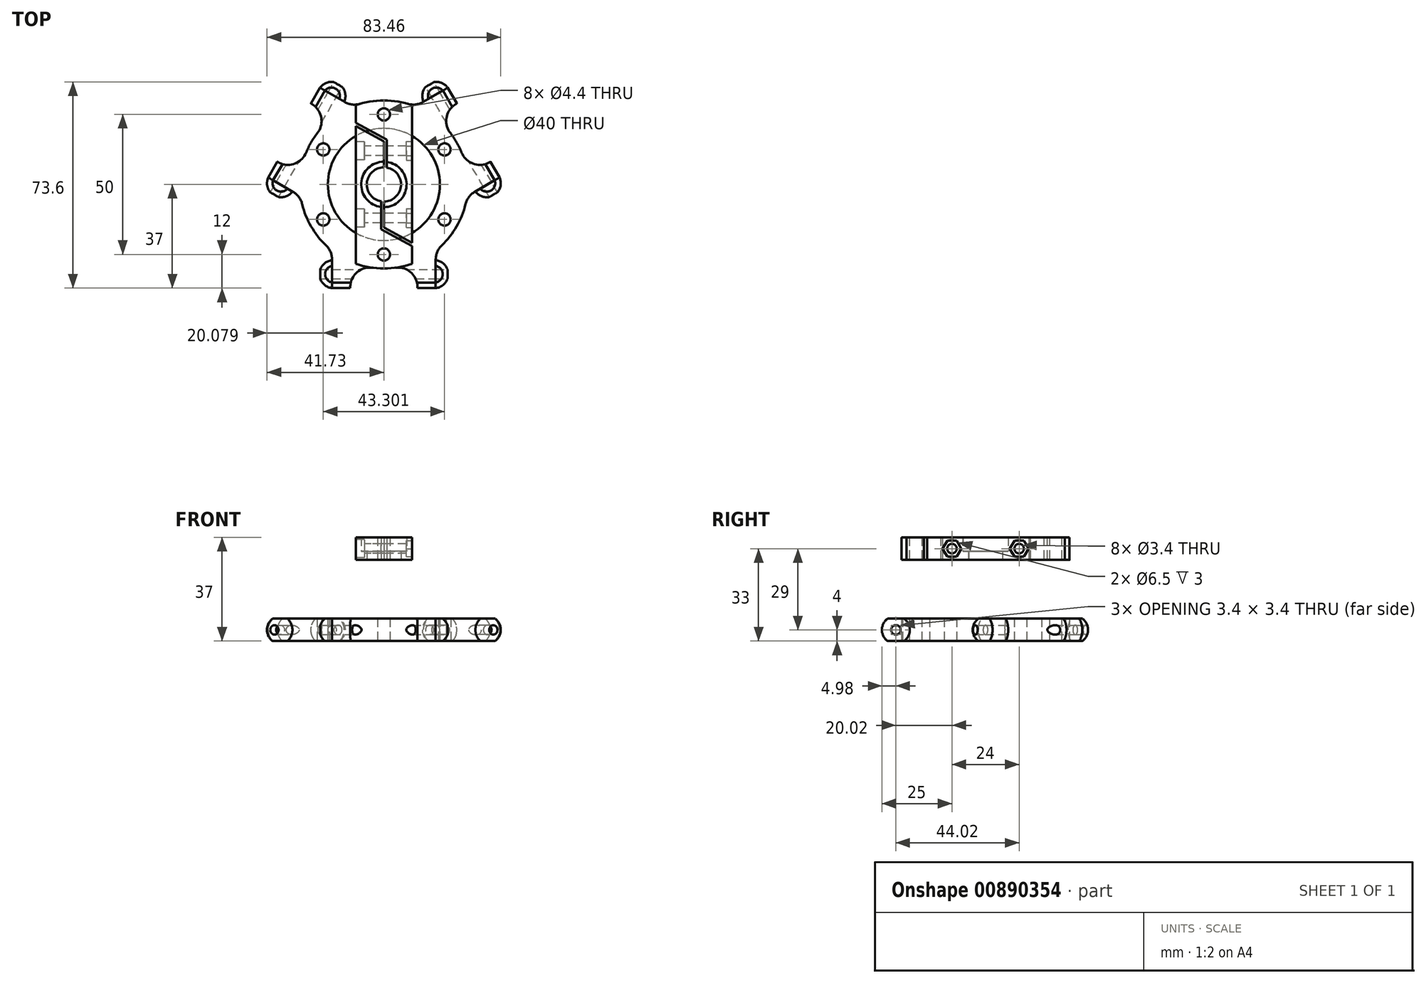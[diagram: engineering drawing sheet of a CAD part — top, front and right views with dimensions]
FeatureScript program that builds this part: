
annotation { "Feature Type Name" : "Feature", "Feature Type Description" : "" }
export const myFeature = defineFeature(function(context is Context, id is Id, definition is map)
    precondition{}
    {
        {
            var Q0;
            Q0=qCreatedBy(makeId("Top.planeOp"),FACE);
            var sketch = newSketch(context, id + "F0", { "sketchPlane" : qUnion([Q0])});
            skLineSegment(sketch, "E0", {"start": v(-16.34, 35.93) * mm, "end": v(-39.06, -3.47) * mm, "construction": true});
            skLineSegment(sketch, "E1", {"start": v(-40.4, -2.74) * mm, "end": v(-37.72, -4.2) * mm, "construction": true});
            skLineSegment(sketch, "E2", {"start": v(-17.63, 36.7) * mm, "end": v(-15.06, 35.15) * mm, "construction": true});
            skCircle(sketch, "E3", {"center": v(0, 0) * mm, "radius": 30 * mm});
            skCircle(sketch, "E4", {"center": v(0, 0) * mm, "radius": 20 * mm});
            skLineSegment(sketch, "E5", {"start": v(0, 0) * mm, "end": v(0, -43.55) * mm, "construction": true});
            skLineSegment(sketch, "E6", {"start": v(-25.45, -32) * mm, "end": v(35.74, -32) * mm, "construction": true});
            skLineSegment(sketch, "E7", {"start": v(-12, -37) * mm, "end": v(-12, -27.5) * mm});
            skLineSegment(sketch, "E8", {"start": v(-12, -37) * mm, "end": v(-18.5, -37) * mm});
            skLineSegment(sketch, "E9", {"start": v(-18.5, -37) * mm, "end": v(-18.5, -23.62) * mm});
            skLineSegment(sketch, "E10.MirrorCS", {"start": v(18.5, -37) * mm, "end": v(18.5, -23.62) * mm});
            skLineSegment(sketch, "E11.MirrorCS", {"start": v(12, -37) * mm, "end": v(12, -27.5) * mm});
            skLineSegment(sketch, "E12.MirrorCS", {"start": v(12, -37) * mm, "end": v(18.5, -37) * mm});
            skLineSegment(sketch, "E13.1.0", {"start": v(41.29, 2.48) * mm, "end": v(29.7, -4.21) * mm});
            skLineSegment(sketch, "E13.1.1", {"start": v(38.04, 8.1) * mm, "end": v(41.29, 2.48) * mm});
            skLineSegment(sketch, "E13.1.2", {"start": v(38.04, 8.1) * mm, "end": v(29.81, 3.36) * mm});
            skLineSegment(sketch, "E13.1.3", {"start": v(26.04, 28.9) * mm, "end": v(17.81, 24.14) * mm});
            skLineSegment(sketch, "E13.1.4", {"start": v(26.04, 28.9) * mm, "end": v(22.79, 34.52) * mm});
            skLineSegment(sketch, "E13.1.5", {"start": v(22.79, 34.52) * mm, "end": v(11.2, 27.83) * mm});
            skLineSegment(sketch, "E13.2.0", {"start": v(-22.79, 34.52) * mm, "end": v(-11.2, 27.83) * mm});
            skLineSegment(sketch, "E13.2.1", {"start": v(-26.04, 28.9) * mm, "end": v(-22.79, 34.52) * mm});
            skLineSegment(sketch, "E13.2.2", {"start": v(-26.04, 28.9) * mm, "end": v(-17.81, 24.14) * mm});
            skLineSegment(sketch, "E13.2.3", {"start": v(-38.04, 8.1) * mm, "end": v(-29.81, 3.36) * mm});
            skLineSegment(sketch, "E13.2.4", {"start": v(-38.04, 8.1) * mm, "end": v(-41.29, 2.48) * mm});
            skLineSegment(sketch, "E13.2.5", {"start": v(-41.29, 2.48) * mm, "end": v(-29.7, -4.21) * mm});
            skCircle(sketch, "E14", {"center": v(0, 25) * mm, "radius": 2.2 * mm});
            skCircle(sketch, "E15.1.0", {"center": v(-21.65, 12.5) * mm, "radius": 2.2 * mm});
            skCircle(sketch, "E15.2.0", {"center": v(-21.65, -12.5) * mm, "radius": 2.2 * mm});
            skCircle(sketch, "E15.3.0", {"center": v(0, -25) * mm, "radius": 2.2 * mm});
            skCircle(sketch, "E15.4.0", {"center": v(21.65, -12.5) * mm, "radius": 2.2 * mm});
            skCircle(sketch, "E15.5.0", {"center": v(21.65, 12.5) * mm, "radius": 2.2 * mm});
            skSolve(sketch);
        }
        {
            var Q0;
            Q0 = qSketchRegion(id + "F0", true);
            extrude(context, id + "F1", {"entities" : qUnion([Q0]), "endBound" : BoundingType.SYMMETRIC, "depth" : 10 * mm, "offsetDistance" : 25 * mm});
        }
        {
            var Q0;
            Q0=qCreatedBy(makeId("Top.planeOp"),FACE);
            var sketch = newSketch(context, id + "F2", { "sketchPlane" : qUnion([Q0])});
            skArc(sketch, "E16", {"start": v(-23, -32.02) * mm, "mid": v(-21.7, -35.37) * mm, "end": v(-18.5, -37) * mm});
            skLineSegment(sketch, "E17", {"start": v(-18, -32.02) * mm, "end": v(-25.15, -32.02) * mm, "construction": true});
            skLineSegment(sketch, "E18", {"start": v(0, 0) * mm, "end": v(0, -44.37) * mm, "construction": true});
            skLineSegment(sketch, "E19", {"start": v(-39.92, 23.05) * mm, "end": v(0, 0) * mm, "construction": true});
            skLineSegment(sketch, "E20", {"start": v(0, 0) * mm, "end": v(41.5, 23.96) * mm, "construction": true});
            skLineSegment(sketch, "E21", {"start": v(-18.5, -37) * mm, "end": v(-18.5, -27.05) * mm});
            skLineSegment(sketch, "E22", {"start": v(-23, -32.02) * mm, "end": v(-18.5, -32.02) * mm});
            skArc(sketch, "E23.1.0", {"start": v(39.23, -3.9) * mm, "mid": v(41.49, -1.11) * mm, "end": v(41.29, 2.48) * mm});
            skLineSegment(sketch, "E23.1.1", {"start": v(39.23, -3.9) * mm, "end": v(36.98, -0.01) * mm});
            skArc(sketch, "E23.2.0", {"start": v(-16.23, 35.93) * mm, "mid": v(-19.78, 36.49) * mm, "end": v(-22.79, 34.52) * mm});
            skLineSegment(sketch, "E23.2.1", {"start": v(-16.23, 35.93) * mm, "end": v(-18.48, 32.03) * mm});
            skPoint(sketch, "E23.center", {"position": v(0, 0) * mm});
            skLineSegment(sketch, "E24.MirrorCS", {"start": v(23, -32.02) * mm, "end": v(18.5, -32.02) * mm});
            skLineSegment(sketch, "E25.MirrorCS", {"start": v(18, -32.02) * mm, "end": v(25.15, -32.02) * mm, "construction": true});
            skLineSegment(sketch, "E26.MirrorCS", {"start": v(18.5, -37) * mm, "end": v(18.5, -27.05) * mm});
            skArc(sketch, "E27.MirrorCS", {"start": v(23, -32.02) * mm, "mid": v(21.7, -35.37) * mm, "end": v(18.5, -37) * mm});
            skSolve(sketch);
        }
        {
            var Q0;
            Q0 = qSketchRegion(id + "F2", true);
            var Q1;
            Q1=sQuery(id+"F2.wireOp",EDGE,"E17");
            revolve(context, id + "F3", {"surfaceOperationType" : NewSurfaceOperationType.NEW, "entities" : qUnion([Q0]), "axis" : qUnion([Q1]), "revolveType" : RevolveType.FULL});
        }
        {
            var Q0;
            Q0=qCreatedBy(makeId("Right.planeOp"),FACE);
            var sketch = newSketch(context, id + "F4", { "sketchPlane" : qUnion([Q0])});
            skLineSegment(sketch, "E28", {"start": v(0, 32.68) * mm, "end": v(0, -16.38) * mm, "construction": true});
            skSolve(sketch);
        }
        {
            var Q0;
            Q0=makeQuery(id+"F3.opRevolve","SWEPT_BODY",BODY,{"disambiguationData":[OSD([sQuery(id+"F2.wireOp",EDGE,"E16"),sQuery(id+"F2.wireOp",EDGE,"E21"),sQuery(id+"F2.wireOp",EDGE,"E22")])]});
            var Q1;
            Q1=makeQuery(id+"F3.opRevolve","SWEPT_BODY",BODY,{"disambiguationData":[OSD([sQuery(id+"F2.wireOp",EDGE,"E24.MirrorCS"),sQuery(id+"F2.wireOp",EDGE,"E26.MirrorCS"),sQuery(id+"F2.wireOp",EDGE,"E27.MirrorCS")])]});
            var Q2;
            Q2=sQuery(id+"F4.wireOp",EDGE,"E28");
            circularPattern(context, id + "F5", {"entities" : qUnion([Q0, Q1]), "axis" : qUnion([Q2]), "angle" : 360 * degree, "instanceCount" : 3, "equalSpace" : true});
        }
        {
            var Q0;
            Q0=makeQuery(id+"F1.opExtrude","CAP_EDGE",EDGE,{"disambiguationData":[OSD([sQuery(id+"F0.wireOp",EDGE,"E13.2.1")])],"isStart":false});
            var Q1;
            Q1=makeQuery(id+"F1.opExtrude","CAP_EDGE",EDGE,{"disambiguationData":[OSD([sQuery(id+"F0.wireOp",EDGE,"E13.2.4")])],"isStart":false});
            var Q2;
            Q2=makeQuery(id+"F1.opExtrude","CAP_EDGE",EDGE,{"disambiguationData":[OSD([sQuery(id+"F0.wireOp",EDGE,"E13.1.4")])],"isStart":false});
            var Q3;
            Q3=makeQuery(id+"F1.opExtrude","CAP_EDGE",EDGE,{"disambiguationData":[OSD([sQuery(id+"F0.wireOp",EDGE,"E13.1.1")])],"isStart":false});
            var Q4;
            Q4=makeQuery(id+"F1.opExtrude","CAP_EDGE",EDGE,{"disambiguationData":[OSD([sQuery(id+"F0.wireOp",EDGE,"E12.MirrorCS")])],"isStart":false});
            var Q5;
            Q5=makeQuery(id+"F1.opExtrude","CAP_EDGE",EDGE,{"disambiguationData":[OSD([sQuery(id+"F0.wireOp",EDGE,"E8")])],"isStart":false});
            var Q6;
            Q6=makeQuery(id+"F1.opExtrude","CAP_EDGE",EDGE,{"disambiguationData":[OSD([sQuery(id+"F0.wireOp",EDGE,"E8")])],"isStart":true});
            var Q7;
            Q7=makeQuery(id+"F1.opExtrude","CAP_EDGE",EDGE,{"disambiguationData":[OSD([sQuery(id+"F0.wireOp",EDGE,"E12.MirrorCS")])],"isStart":true});
            var Q8;
            Q8=makeQuery(id+"F1.opExtrude","CAP_EDGE",EDGE,{"disambiguationData":[OSD([sQuery(id+"F0.wireOp",EDGE,"E13.1.1")])],"isStart":true});
            var Q9;
            Q9=makeQuery(id+"F1.opExtrude","CAP_EDGE",EDGE,{"disambiguationData":[OSD([sQuery(id+"F0.wireOp",EDGE,"E13.1.4")])],"isStart":true});
            var Q10;
            Q10=makeQuery(id+"F1.opExtrude","CAP_EDGE",EDGE,{"disambiguationData":[OSD([sQuery(id+"F0.wireOp",EDGE,"E13.2.1")])],"isStart":true});
            var Q11;
            Q11=makeQuery(id+"F1.opExtrude","CAP_EDGE",EDGE,{"disambiguationData":[OSD([sQuery(id+"F0.wireOp",EDGE,"E13.2.4")])],"isStart":true});
            fillet(context, id + "F6", {"entities" : qUnion([Q0, Q1, Q2, Q3, Q4, Q5, Q6, Q7, Q8, Q9, Q10, Q11]), "radius" : 5 * mm, "tangentPropagation" : true, "allowEdgeOverflow" : false});
        }
        {
            var Q0;
            Q0=qCreatedBy(makeId("Top.planeOp"),FACE);
            var sketch = newSketch(context, id + "F7", { "sketchPlane" : qUnion([Q0])});
            skCircle(sketch, "E29", {"center": v(0, 0) * mm, "radius": 54.32 * mm});
            skSolve(sketch);
        }
        {
            var Q0;
            Q0=makeQuery(id+"F7.imprint","IMPRINT",FACE,{"disambiguationData":[TD([[makeQuery(id+"F7.imprint","IMPRINT",EDGE,{"derivedFrom":sQuery(id+"F7.wireOp",EDGE,"E29")}),1.0]])]});
            extrude(context, id + "F8", {"entities" : qUnion([Q0]), "operationType" : NewBodyOperationType.REMOVE, "depth" : 10 * mm, "offsetDistance" : 25 * mm, "hasSecondDirection" : true, "secondDirectionOppositeDirection" : false, "secondDirectionDepth" : 4 * mm});
        }
        {
            var Q0;
            Q0=makeQuery(id+"F7.imprint","IMPRINT",FACE,{"disambiguationData":[TD([[makeQuery(id+"F7.imprint","IMPRINT",EDGE,{"derivedFrom":sQuery(id+"F7.wireOp",EDGE,"E29")}),1.0]])]});
            extrude(context, id + "F9", {"entities" : qUnion([Q0]), "operationType" : NewBodyOperationType.REMOVE, "oppositeDirection" : true, "depth" : 20 * mm, "offsetDistance" : 25 * mm, "hasSecondDirection" : true, "secondDirectionOppositeDirection" : true, "secondDirectionDepth" : 4 * mm});
        }
        {
            var Q0;
            Q0=qCreatedBy(makeId("Right.planeOp"),FACE);
            var sketch = newSketch(context, id + "F10", { "sketchPlane" : qUnion([Q0])});
            skCircle(sketch, "E30", {"center": v(-32.02, 0) * mm, "radius": 1.7 * mm});
            skSolve(sketch);
        }
        {
            var Q0;
            Q0 = qSketchRegion(id + "F10", true);
            extrude(context, id + "F11", {"entities" : qUnion([Q0]), "operationType" : NewBodyOperationType.REMOVE, "endBound" : BoundingType.SYMMETRIC, "oppositeDirection" : true, "depth" : 80 * mm, "offsetDistance" : 25 * mm});
        }
        {
            var Q0;
            Q0=sQuery(id+"F2.wireOp",EDGE,"E19");
            cPlane(context, id + "F12", {"entities" : qUnion([Q0]), "cplaneType" : CPlaneType.LINE_ANGLE, "offset" : 25 * mm, "angle" : 0 * degree, "width" : 150 * mm, "height" : 150 * mm});
        }
        {
            var Q0;
            Q0=qCreatedBy(id+"F12.planeOp",FACE);
            var sketch = newSketch(context, id + "F13", { "sketchPlane" : qUnion([Q0])});
            skCircle(sketch, "E31", {"center": v(32.02, 0) * mm, "radius": 1.7 * mm});
            skSolve(sketch);
        }
        {
            var Q0;
            Q0 = qSketchRegion(id + "F13", true);
            extrude(context, id + "F14", {"entities" : qUnion([Q0]), "operationType" : NewBodyOperationType.REMOVE, "endBound" : BoundingType.SYMMETRIC, "oppositeDirection" : true, "depth" : 80 * mm, "offsetDistance" : 25 * mm});
        }
        {
            var Q0;
            Q0=sQuery(id+"F2.wireOp",EDGE,"E20");
            cPlane(context, id + "F15", {"entities" : qUnion([Q0]), "cplaneType" : CPlaneType.LINE_ANGLE, "offset" : 25 * mm, "angle" : 0 * degree, "width" : 150 * mm, "height" : 150 * mm});
        }
        {
            var Q0;
            Q0=qCreatedBy(id+"F15.planeOp",FACE);
            var sketch = newSketch(context, id + "F16", { "sketchPlane" : qUnion([Q0])});
            skCircle(sketch, "E32", {"center": v(-32.02, 0) * mm, "radius": 1.7 * mm});
            skSolve(sketch);
        }
        {
            var Q0;
            Q0 = qSketchRegion(id + "F16", true);
            extrude(context, id + "F17", {"entities" : qUnion([Q0]), "operationType" : NewBodyOperationType.REMOVE, "endBound" : BoundingType.SYMMETRIC, "oppositeDirection" : true, "depth" : 80 * mm, "offsetDistance" : 25 * mm});
        }
        {
            var Q0;
            Q0=makeQuery(id+"F1.opExtrude","SWEPT_EDGE",EDGE,{"disambiguationData":[OSD([sQuery(id+"F0.wireOp",EDGE,"E3"),sQuery(id+"F0.wireOp",EDGE,"E13.2.0")])]});
            var Q1;
            Q1=makeQuery(id+"F1.opExtrude","SWEPT_EDGE",EDGE,{"disambiguationData":[OSD([sQuery(id+"F0.wireOp",EDGE,"E3"),sQuery(id+"F0.wireOp",EDGE,"E13.1.5")])]});
            var Q2;
            Q2=makeQuery(id+"F1.opExtrude","SWEPT_EDGE",EDGE,{"disambiguationData":[OSD([sQuery(id+"F0.wireOp",EDGE,"E3"),sQuery(id+"F0.wireOp",EDGE,"E13.1.0")])]});
            var Q3;
            Q3=makeQuery(id+"F1.opExtrude","SWEPT_EDGE",EDGE,{"disambiguationData":[OSD([sQuery(id+"F0.wireOp",EDGE,"E3"),sQuery(id+"F0.wireOp",EDGE,"E10.MirrorCS")])]});
            var Q4;
            Q4=makeQuery(id+"F1.opExtrude","SWEPT_EDGE",EDGE,{"disambiguationData":[OSD([sQuery(id+"F0.wireOp",EDGE,"E3"),sQuery(id+"F0.wireOp",EDGE,"E13.2.5")])]});
            var Q5;
            Q5=makeQuery(id+"F1.opExtrude","SWEPT_EDGE",EDGE,{"disambiguationData":[OSD([sQuery(id+"F0.wireOp",EDGE,"E3"),sQuery(id+"F0.wireOp",EDGE,"E9")])]});
            fillet(context, id + "F18", {"entities" : qUnion([Q0, Q1, Q2, Q3, Q4, Q5]), "radius" : 7 * mm, "tangentPropagation" : true, "allowEdgeOverflow" : false});
        }
        {
            var Q0;
            Q0=qCreatedBy(makeId("Top.planeOp"),FACE);
            cPlane(context, id + "F19", {"entities" : qUnion([Q0]), "cplaneType" : CPlaneType.OFFSET, "offset" : 25 * mm, "width" : 150 * mm, "height" : 150 * mm});
        }
        {
            var Q0;
            Q0=qCreatedBy(id+"F19.planeOp",FACE);
            var sketch = newSketch(context, id + "F20", { "sketchPlane" : qUnion([Q0])});
            skCircle(sketch, "E33", {"center": v(0, 25) * mm, "radius": 2.2 * mm});
            skCircle(sketch, "E34", {"center": v(0, -25) * mm, "radius": 2.2 * mm});
            skArc(sketch, "E35", {"start": v(10, 28.28) * mm, "mid": v(0, 30) * mm, "end": v(-10, 28.28) * mm});
            skLineSegment(sketch, "E36", {"start": v(-10, 28.28) * mm, "end": v(-10, -28.28) * mm});
            skLineSegment(sketch, "E37", {"start": v(10, -28.28) * mm, "end": v(10, 28.28) * mm});
            skArc(sketch, "E38.trimOffspring", {"start": v(-10, -28.28) * mm, "mid": v(0, -30) * mm, "end": v(10, -28.28) * mm});
            skSolve(sketch);
        }
        {
            var Q0;
            Q0=makeQuery(id+"F20.imprint","IMPRINT",FACE,{"disambiguationData":[TD([[makeQuery(id+"F20.imprint","IMPRINT",EDGE,{"derivedFrom":sQuery(id+"F20.wireOp",EDGE,"E33")}),-1.0]])]});
            extrude(context, id + "F21", {"entities" : qUnion([Q0]), "depth" : 8 * mm, "offsetDistance" : 25 * mm});
        }
        {
            var Q0;
            Q0=makeQuery(id+"F21.opExtrude","CAP_FACE",FACE,{"disambiguationData":[OSD([sQuery(id+"F20.wireOp",EDGE,"E33"),sQuery(id+"F20.wireOp",EDGE,"E34"),sQuery(id+"F20.wireOp",EDGE,"E35"),sQuery(id+"F20.wireOp",EDGE,"E36"),sQuery(id+"F20.wireOp",EDGE,"E37"),sQuery(id+"F20.wireOp",EDGE,"E38.trimOffspring")])],"isStart":true});
            var sketch = newSketch(context, id + "F22", { "sketchPlane" : qUnion([Q0])});
            skCircle(sketch, "E39", {"center": v(0, 0) * mm, "radius": 6.1 * mm});
            skCircle(sketch, "E40", {"center": v(0, 0) * mm, "radius": 8.1 * mm});
            skLineSegment(sketch, "E41", {"start": v(-10, -20.86) * mm, "end": v(0, -15.4) * mm});
            skLineSegment(sketch, "E42", {"start": v(1, 0) * mm, "end": v(1, -16) * mm});
            skLineSegment(sketch, "E43", {"start": v(1, -16) * mm, "end": v(-10, -22) * mm});
            skLineSegment(sketch, "E44", {"start": v(-10, -22) * mm, "end": v(10, -22) * mm, "construction": true});
            skLineSegment(sketch, "E45", {"start": v(-10, -22) * mm, "end": v(-10, -20.86) * mm});
            skLineSegment(sketch, "E46", {"start": v(0, -15.4) * mm, "end": v(0, 0) * mm});
            skLineSegment(sketch, "E47", {"start": v(0, 0) * mm, "end": v(1, 0) * mm});
            skLineSegment(sketch, "E48.1.0", {"start": v(10, 22) * mm, "end": v(10, 20.86) * mm});
            skLineSegment(sketch, "E48.1.1", {"start": v(10, 20.86) * mm, "end": v(0, 15.4) * mm});
            skLineSegment(sketch, "E48.1.2", {"start": v(-1, 16) * mm, "end": v(10, 22) * mm});
            skLineSegment(sketch, "E48.1.3", {"start": v(0, 15.4) * mm, "end": v(0, 0) * mm});
            skLineSegment(sketch, "E48.1.4", {"start": v(-1, 0) * mm, "end": v(-1, 16) * mm});
            skLineSegment(sketch, "E48.1.5", {"start": v(0, 0) * mm, "end": v(-1, 0) * mm});
            skSolve(sketch);
        }
        {
            var Q0;
            Q0=makeQuery(id+"F22.imprint","IMPRINT",FACE,{"disambiguationData":[TD([[makeQuery(id+"F22.imprint","IMPRINT",EDGE,{"derivedFrom":sQuery(id+"F22.wireOp",EDGE,"E39")}),1.0]])]});
            var Q1;
            Q1=makeQuery(id+"F21.opExtrude","CAP_FACE",FACE,{"disambiguationData":[OSD([sQuery(id+"F20.wireOp",EDGE,"E33"),sQuery(id+"F20.wireOp",EDGE,"E34"),sQuery(id+"F20.wireOp",EDGE,"E35"),sQuery(id+"F20.wireOp",EDGE,"E36"),sQuery(id+"F20.wireOp",EDGE,"E37"),sQuery(id+"F20.wireOp",EDGE,"E38.trimOffspring")])],"isStart":false});
            extrude(context, id + "F23", {"entities" : qUnion([Q0]), "operationType" : NewBodyOperationType.REMOVE, "endBound" : BoundingType.UP_TO_SURFACE, "oppositeDirection" : true, "depth" : 25 * mm, "endBoundEntityFace" : qUnion([Q1]), "offsetDistance" : 25 * mm});
        }
        {
            var Q0;
            Q0=makeQuery(id+"F22.imprint","IMPRINT",FACE,{"disambiguationData":[TD([[makeQuery(id+"F22.imprint","IMPRINT",EDGE,{"derivedFrom":sQuery(id+"F22.wireOp",EDGE,"E48.1.0")}),-1.0]])]});
            var Q1;
            {var subQ0=sQuery(id+"F22.wireOp",EDGE,"E48.1.4");var subQ1=sQuery(id+"F22.wireOp",EDGE,"E39");var subQ2=makeQuery(id+"F22.imprint","INTERSECT",VERTEX,{"derivedFrom":[subQ1,subQ0]});Q1=makeQuery(id+"F22.imprint","IMPRINT",FACE,{"disambiguationData":[TD([[makeQuery(id+"F22.imprint","IMPRINT",EDGE,{"disambiguationData":[TD([[subQ2,1.0]])],"derivedFrom":subQ1}),-1.0]])]});}
            var Q2;
            {var subQ1=sQuery(id+"F22.wireOp",EDGE,"E41");Q2=makeQuery(id+"F22.imprint","IMPRINT",FACE,{"disambiguationData":[TD([[makeQuery(id+"F22.imprint","IMPRINT",EDGE,{"derivedFrom":subQ1}),-1.0]])]});}
            var Q3;
            {var subQ0=sQuery(id+"F22.wireOp",EDGE,"E46");var subQ1=sQuery(id+"F22.wireOp",EDGE,"E39");var subQ2=makeQuery(id+"F22.imprint","INTERSECT",VERTEX,{"derivedFrom":[subQ1,subQ0]});Q3=makeQuery(id+"F22.imprint","IMPRINT",FACE,{"disambiguationData":[TD([[makeQuery(id+"F22.imprint","IMPRINT",EDGE,{"disambiguationData":[TD([[subQ2,-1.0]])],"derivedFrom":subQ1}),-1.0]])]});}
            var Q4;
            Q4=makeQuery(id+"F21.opExtrude","CAP_FACE",FACE,{"disambiguationData":[OSD([sQuery(id+"F20.wireOp",EDGE,"E33"),sQuery(id+"F20.wireOp",EDGE,"E34"),sQuery(id+"F20.wireOp",EDGE,"E35"),sQuery(id+"F20.wireOp",EDGE,"E36"),sQuery(id+"F20.wireOp",EDGE,"E37"),sQuery(id+"F20.wireOp",EDGE,"E38.trimOffspring")])],"isStart":false});
            extrude(context, id + "F24", {"entities" : qUnion([Q0, Q1, Q2, Q3]), "operationType" : NewBodyOperationType.REMOVE, "endBound" : BoundingType.UP_TO_SURFACE, "oppositeDirection" : true, "depth" : 25 * mm, "endBoundEntityFace" : qUnion([Q4]), "offsetDistance" : 25 * mm});
        }
        {
            var Q0;
            {var subQ3=sQuery(id+"F22.wireOp",EDGE,"00b420b3-74bb-4662-af47-3d81f60943aa.1.3");var subQ5=sQuery(id+"F22.wireOp",EDGE,"E40");var subQ6=makeQuery(id+"F22.imprint","INTERSECT",VERTEX,{"derivedFrom":[subQ5,subQ3]});Q0=makeQuery(id+"F22.imprint","IMPRINT",FACE,{"disambiguationData":[TD([[makeQuery(id+"F22.imprint","IMPRINT",EDGE,{"disambiguationData":[TD([[subQ6,-1.0]])],"derivedFrom":subQ5}),1.0]])]});}
            var Q1;
            {var subQ3=sQuery(id+"F22.wireOp",EDGE,"00b420b3-74bb-4662-af47-3d81f60943aa.1.2");var subQ5=sQuery(id+"F22.wireOp",EDGE,"E40");var subQ6=makeQuery(id+"F22.imprint","INTERSECT",VERTEX,{"derivedFrom":[subQ5,subQ3]});Q1=makeQuery(id+"F22.imprint","IMPRINT",FACE,{"disambiguationData":[TD([[makeQuery(id+"F22.imprint","IMPRINT",EDGE,{"disambiguationData":[TD([[subQ6,1.0]])],"derivedFrom":subQ5}),1.0]])]});}
            extrude(context, id + "F25", {"entities" : qUnion([Q0, Q1]), "operationType" : NewBodyOperationType.REMOVE, "oppositeDirection" : true, "depth" : 20 * mm, "offsetDistance" : 25 * mm, "hasSecondDirection" : true, "secondDirectionOppositeDirection" : true, "secondDirectionDepth" : 3 * mm});
        }
        {
            var Q0;
            {var subQ0=sQuery(id+"F20.wireOp",EDGE,"E38.trimOffspring");var subQ2=sQuery(id+"F20.wireOp",EDGE,"E36");Q0=makeQuery(id+"F24.boolean.opBoolean","SPLIT",FACE,{"disambiguationData":[TD([makeQuery(id+"F21.opExtrude","SWEPT_FACE",FACE,{"disambiguationData":[OSD([subQ0])]})])],"derivedFrom":makeQuery(id+"F21.opExtrude","SWEPT_FACE",FACE,{"disambiguationData":[OSD([subQ2])]})});}
            var sketch = newSketch(context, id + "F26", { "sketchPlane" : qUnion([Q0])});
            skPoint(sketch, "E49", {"position": v(-12, 29) * mm});
            skPoint(sketch, "E49.positionSnap0", {"position": v(-20.86, 29) * mm});
            skPoint(sketch, "E50", {"position": v(12, 29) * mm});
            skSolve(sketch);
        }
        {
            var Q0;
            Q0=sQuery(id+"F26.wireOp",VERTEX,"E49");
            var Q1;
            Q1=sQuery(id+"F26.wireOp",VERTEX,"E50");
            var Q2;
            Q2=makeQuery(id+"F24.boolean.opBoolean","SPLIT",BODY,{"disambiguationData":[OD(0.0)],"derivedFrom":makeQuery(id+"F21.opExtrude","SWEPT_BODY",BODY,{"disambiguationData":[OSD([sQuery(id+"F20.wireOp",EDGE,"E33"),sQuery(id+"F20.wireOp",EDGE,"E34"),sQuery(id+"F20.wireOp",EDGE,"E35"),sQuery(id+"F20.wireOp",EDGE,"E36"),sQuery(id+"F20.wireOp",EDGE,"E37"),sQuery(id+"F20.wireOp",EDGE,"E38.trimOffspring")])]})});
            var Q3;
            Q3=makeQuery(id+"F24.boolean.opBoolean","SPLIT",BODY,{"disambiguationData":[OD(1.0)],"derivedFrom":makeQuery(id+"F21.opExtrude","SWEPT_BODY",BODY,{"disambiguationData":[OSD([sQuery(id+"F20.wireOp",EDGE,"E33"),sQuery(id+"F20.wireOp",EDGE,"E34"),sQuery(id+"F20.wireOp",EDGE,"E35"),sQuery(id+"F20.wireOp",EDGE,"E36"),sQuery(id+"F20.wireOp",EDGE,"E37"),sQuery(id+"F20.wireOp",EDGE,"E38.trimOffspring")])]})});
            hole(context, id + "F27", {"style" : HoleStyle.C_BORE, "endStyle" : HoleEndStyle.THROUGH, "standardTappedOrClearance" : lookupTablePath({ "fit" : "Normal", "standard" : "ISO", "size" : "M3", "type" : "Clearance" }), "standardBlindInLast" : lookupTablePath({ "fit" : "Normal", "standard" : "ISO", "size" : "M3", "type" : "Clearance" }), "holeDiameter" : 3.4 * mm, "cBoreDiameter" : 6.5 * mm, "cBoreDepth" : 3 * mm, "majorDiameter" : 5 * mm, "isTappedThrough" : true, "tappedDepth" : 12 * mm, "tapClearance" : 3, "locations" : qUnion([Q0, Q1]), "scope" : qUnion([Q2, Q3])});
        }
        {
            var Q0;
            {var subQ1=sQuery(id+"F20.wireOp",EDGE,"E37");var subQ3=sQuery(id+"F20.wireOp",EDGE,"E35");Q0=makeQuery(id+"F24.boolean.opBoolean","SPLIT",FACE,{"disambiguationData":[TD([makeQuery(id+"F21.opExtrude","SWEPT_FACE",FACE,{"disambiguationData":[OSD([subQ3])]})])],"derivedFrom":makeQuery(id+"F21.opExtrude","SWEPT_FACE",FACE,{"disambiguationData":[OSD([subQ1])]})});}
            var sketch = newSketch(context, id + "F28", { "sketchPlane" : qUnion([Q0])});
            skCircle(sketch, "E51.cCircle", {"center": v(-12, 29) * mm, "radius": 2.9 * mm, "construction": true});
            skLineSegment(sketch, "E51.0", {"start": v(-10.33, 26.1) * mm, "end": v(-13.67, 26.1) * mm});
            skLineSegment(sketch, "E51.1", {"start": v(-13.67, 26.1) * mm, "end": v(-15.35, 29) * mm});
            skLineSegment(sketch, "E51.2", {"start": v(-15.35, 29) * mm, "end": v(-13.67, 31.9) * mm});
            skLineSegment(sketch, "E51.3", {"start": v(-13.67, 31.9) * mm, "end": v(-10.33, 31.9) * mm});
            skLineSegment(sketch, "E51.4", {"start": v(-10.33, 31.9) * mm, "end": v(-8.65, 29) * mm});
            skLineSegment(sketch, "E51.5", {"start": v(-8.65, 29) * mm, "end": v(-10.33, 26.1) * mm});
            skPoint(sketch, "E51.0.midPoint", {"position": v(-12, 26.1) * mm});
            skLineSegment(sketch, "E52.MirrorCS", {"start": v(10.33, 26.1) * mm, "end": v(13.67, 26.1) * mm});
            skLineSegment(sketch, "E53.MirrorCS", {"start": v(13.67, 31.9) * mm, "end": v(10.33, 31.9) * mm});
            skLineSegment(sketch, "E54.MirrorCS", {"start": v(13.67, 26.1) * mm, "end": v(15.35, 29) * mm});
            skLineSegment(sketch, "E55.MirrorCS", {"start": v(10.33, 31.9) * mm, "end": v(8.65, 29) * mm});
            skLineSegment(sketch, "E56.MirrorCS", {"start": v(15.35, 29) * mm, "end": v(13.67, 31.9) * mm});
            skCircle(sketch, "E57.MirrorC", {"center": v(12, 29) * mm, "radius": 2.9 * mm, "construction": true});
            skPoint(sketch, "E58.MirrorP", {"position": v(12, 26.1) * mm});
            skLineSegment(sketch, "E59.MirrorCS", {"start": v(8.65, 29) * mm, "end": v(10.33, 26.1) * mm});
            skSolve(sketch);
        }
        {
            var Q0;
            Q0 = qSketchRegion(id + "F28", true);
            extrude(context, id + "F29", {"entities" : qUnion([Q0]), "operationType" : NewBodyOperationType.REMOVE, "oppositeDirection" : true, "depth" : 2 * mm, "offsetDistance" : 25 * mm});
        }
    });
